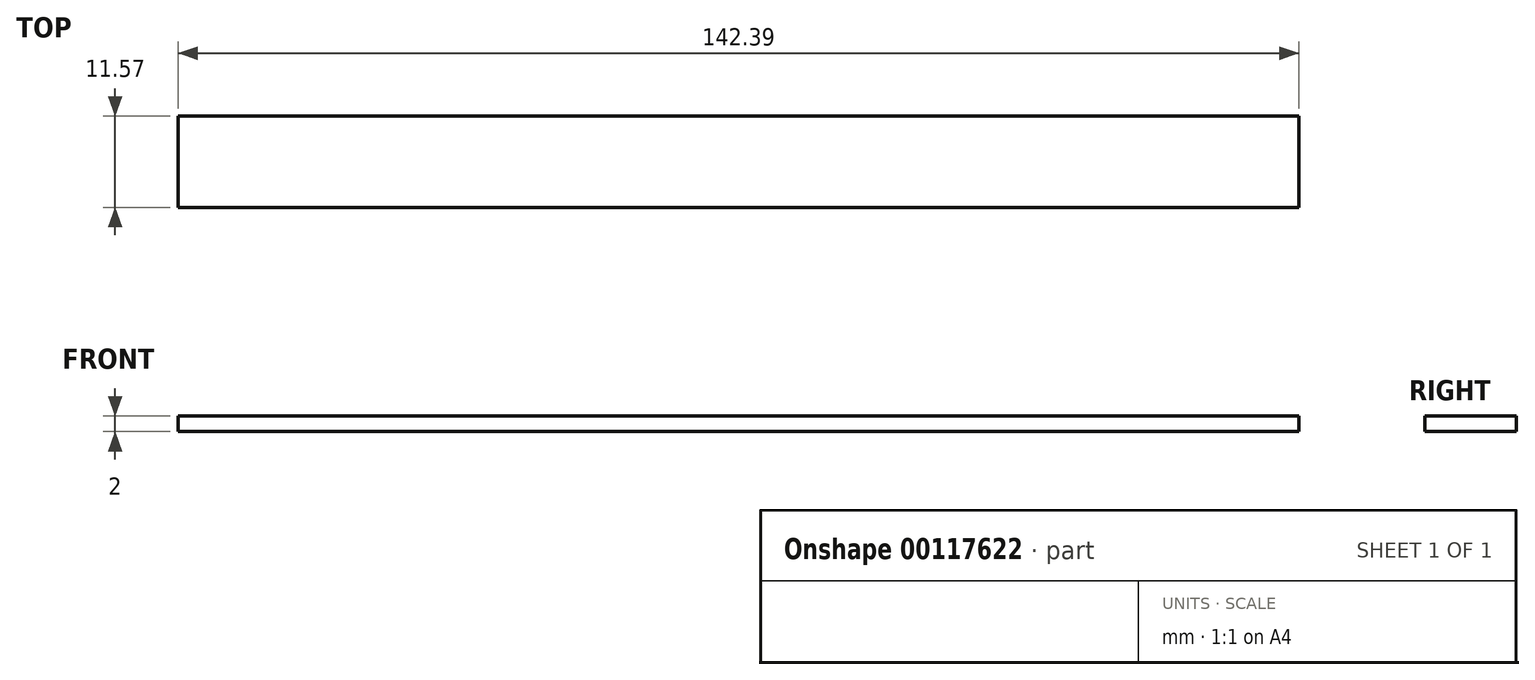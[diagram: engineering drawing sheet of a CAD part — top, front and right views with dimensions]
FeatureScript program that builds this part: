
annotation { "Feature Type Name" : "Feature", "Feature Type Description" : "" }
export const myFeature = defineFeature(function(context is Context, id is Id, definition is map)
    precondition{}
    {
        {
            var Q0;
            Q0=qCreatedBy(makeId("Top.planeOp"),FACE);
            var sketch = newSketch(context, id + "F0", { "sketchPlane" : qUnion([Q0])});
            skLineSegment(sketch, "E0.bottom", {"start": v(-71.31, 9.56) * mm, "end": v(71.08, 9.56) * mm});
            skLineSegment(sketch, "E0.top", {"start": v(-71.31, -2) * mm, "end": v(71.08, -2) * mm});
            skLineSegment(sketch, "E0.left", {"start": v(-71.31, 9.56) * mm, "end": v(-71.31, -2) * mm});
            skLineSegment(sketch, "E0.right", {"start": v(71.08, 9.56) * mm, "end": v(71.08, -2) * mm});
            skSolve(sketch);
        }
        {
            var Q0;
            Q0=makeQuery(id+"F0.imprint","IMPRINT",FACE,{"disambiguationData":[TD([[makeQuery(id+"F0.imprint","IMPRINT",EDGE,{"derivedFrom":sQuery(id+"F0.wireOp",EDGE,"E0.bottom")}),-1.0]])]});
            extrude(context, id + "F1", {"entities" : qUnion([Q0]), "depth" : 2 * mm});
        }
    });
